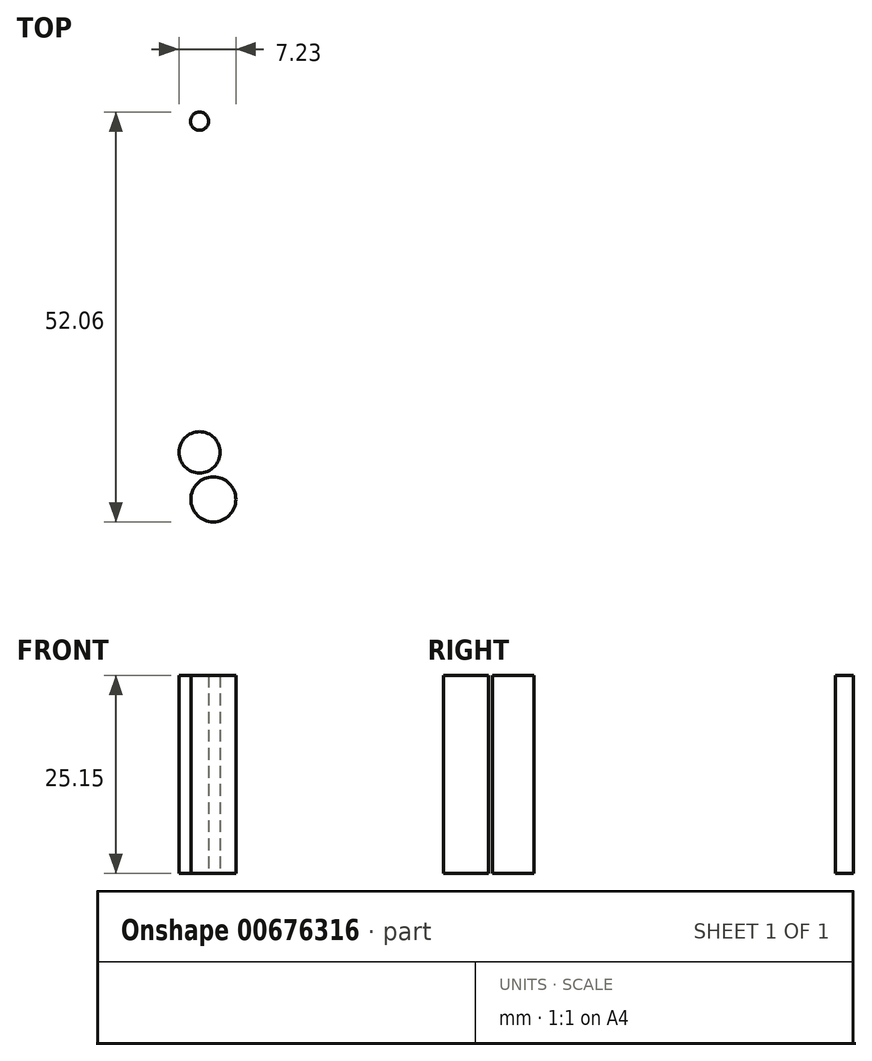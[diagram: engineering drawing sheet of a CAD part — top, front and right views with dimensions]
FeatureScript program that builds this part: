
annotation { "Feature Type Name" : "Feature", "Feature Type Description" : "" }
export const myFeature = defineFeature(function(context is Context, id is Id, definition is map)
    precondition{}
    {
        {
            var Q0;
            Q0=qCreatedBy(makeId("Top.planeOp"),FACE);
            var sketch = newSketch(context, id + "F0", { "sketchPlane" : qUnion([Q0])});
            skCircle(sketch, "E0", {"center": v(0, 39.54) * mm, "radius": 1.15 * mm});
            skCircle(sketch, "E1", {"center": v(0, -2.52) * mm, "radius": 2.62 * mm});
            skCircle(sketch, "E2", {"center": v(1.76, -8.5) * mm, "radius": 2.86 * mm});
            skSolve(sketch);
        }
        {
            var Q0;
            Q0 = qSketchRegion(id + "F0", true);
            extrude(context, id + "F1", {"entities" : qUnion([Q0]), "depth" : 25.15 * mm, "offsetDistance" : 25.4 * mm});
        }
    });
